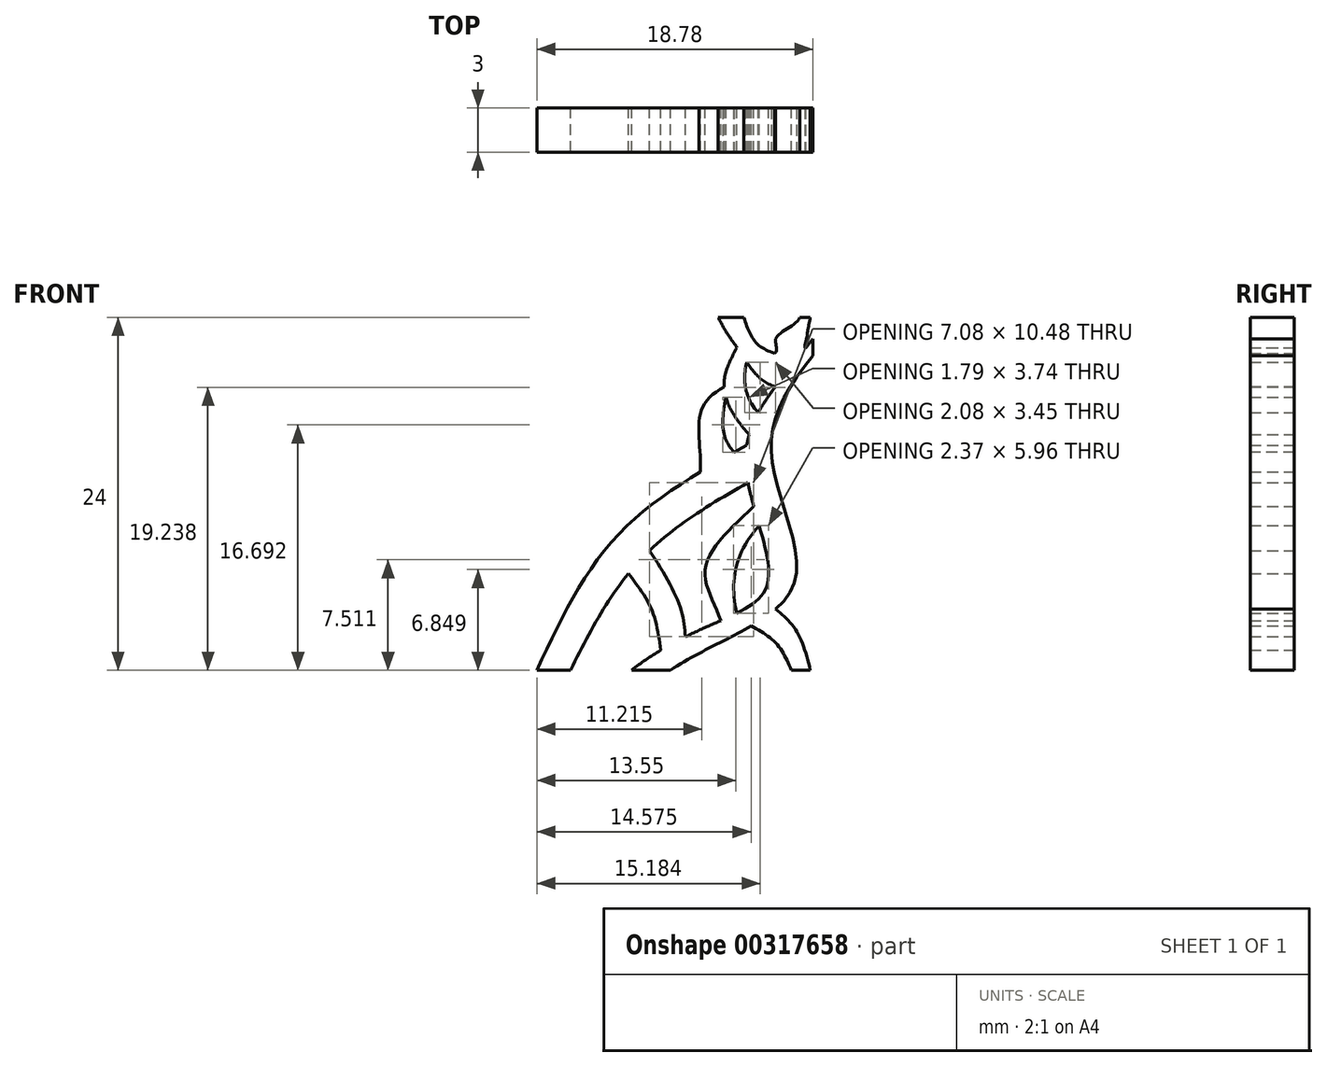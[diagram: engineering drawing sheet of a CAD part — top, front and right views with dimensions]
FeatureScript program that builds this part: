
annotation { "Feature Type Name" : "Feature", "Feature Type Description" : "" }
export const myFeature = defineFeature(function(context is Context, id is Id, definition is map)
    precondition{}
    {
        {
            var Q0;
            Q0=qCreatedBy(makeId("Front.planeOp"),FACE);
            var sketch = newSketch(context, id + "F0", { "sketchPlane" : qUnion([Q0])});
            skLineSegment(sketch, "E0.bottom", {"start": v(161.57, 207.7) * mm, "end": v(-151.57, 207.7) * mm});
            skLineSegment(sketch, "E0.top", {"start": v(161.57, -192.3) * mm, "end": v(-151.57, -192.3) * mm});
            skLineSegment(sketch, "E0.left", {"start": v(161.57, 207.7) * mm, "end": v(161.57, -192.3) * mm});
            skLineSegment(sketch, "E0.right", {"start": v(-151.57, 207.7) * mm, "end": v(-151.57, -192.3) * mm});
            skFitSpline(sketch, "E1", {"points": [v(161.57, 183.5) * mm, v(85.12, 44.75) * mm, v(109.31, -96.4) * mm, v(-44.12, -192.3) * mm], "startDerivative": vector(-382, -492.17) * mm, "endDerivative": vector(-632.26, -490) * mm});
            skFitSpline(sketch, "E2", {"points": [v(161.57, 164.23) * mm, v(115.12, 45.06) * mm, v(139.33, -96.46) * mm, v(0, -192.3) * mm], "startDerivative": vector(-323.93, -389.82) * mm, "endDerivative": vector(-432.8, -289.86) * mm});
            skFitSpline(sketch, "E3", {"points": [v(87.95, 20.15) * mm, v(-36.08, -69.46) * mm, v(-113.36, -192.3) * mm], "startDerivative": vector(-287.2, -159.14) * mm, "endDerivative": vector(-134.26, -271.05) * mm});
            skFitSpline(sketch, "E4", {"points": [v(86.4, 62.77) * mm, v(-60.96, -40.6) * mm, v(-151.57, -192.3) * mm], "startDerivative": vector(-322.1, -181.09) * mm, "endDerivative": vector(-154.33, -329.73) * mm});
            skFitSpline(sketch, "E5", {"points": [v(91.66, -142.16) * mm, v(120.33, -162.57) * mm, v(137.1, -192.3) * mm], "startDerivative": vector(63.12, -36.39) * mm, "endDerivative": vector(28.09, -64.9) * mm});
            skFitSpline(sketch, "E6", {"points": [v(119.32, -123.08) * mm, v(142.68, -147.67) * mm, v(158.5, -192.3) * mm], "startDerivative": vector(55.7, -46.78) * mm, "endDerivative": vector(23.32, -90.23) * mm});
            skFitSpline(sketch, "E7", {"points": [v(100.65, -28.51) * mm, v(73.78, -78.77) * mm, v(75.03, -127.85) * mm], "startDerivative": vector(-88.91, -98.41) * mm, "endDerivative": vector(24.95, -113.83) * mm});
            skFitSpline(sketch, "E8", {"points": [v(94.41, -6.72) * mm, v(39.45, -75.98) * mm, v(57.07, -136.12) * mm], "startDerivative": vector(-135.48, -128.88) * mm, "endDerivative": vector(50.2, -141.27) * mm});
            skFitSpline(sketch, "E9", {"points": [v(54.23, 207.7) * mm, v(81.23, 165.16) * mm, v(119.4, 129.17) * mm], "startDerivative": vector(44.56, -99.42) * mm, "endDerivative": vector(118.17, -31.75) * mm});
            skFitSpline(sketch, "E10", {"points": [v(83.1, 207.7) * mm, v(99.85, 176.33) * mm, v(142.84, 159.86) * mm], "startDerivative": vector(25.78, -76.02) * mm, "endDerivative": vector(99.84, -29.98) * mm});
            skFitSpline(sketch, "E11", {"points": [v(146.4, 207.7) * mm, v(119.4, 183.78) * mm, v(118, 167.02) * mm], "startDerivative": vector(-16.59, -50.41) * mm, "endDerivative": vector(-40.58, -34) * mm});
            skFitSpline(sketch, "E12", {"points": [v(158.5, 207.7) * mm, v(153.85, 181.92) * mm, v(152.97, 172.55) * mm], "startDerivative": vector(-12.64, -48.27) * mm, "endDerivative": vector(10.98, -30.7) * mm});
            skFitSpline(sketch, "E13", {"points": [v(75.43, 173.52) * mm, v(60.75, 128.85) * mm, v(89.2, 75) * mm], "startDerivative": vector(-54.24, -96.72) * mm, "endDerivative": vector(96.14, -103.87) * mm});
            skFitSpline(sketch, "E14", {"points": [v(86.56, 157.05) * mm, v(84.95, 128.85) * mm, v(99.53, 99.55) * mm], "startDerivative": vector(-16.02, -62.32) * mm, "endDerivative": vector(51.54, -60.1) * mm});
            skFitSpline(sketch, "E15", {"points": [v(62.75, 117) * mm, v(60.75, 74.85) * mm, v(72.13, 54.72) * mm], "startDerivative": vector(-16.42, -83.23) * mm, "endDerivative": vector(39.32, -49.75) * mm});
            skFitSpline(sketch, "E16", {"points": [v(60.75, 128.85) * mm, v(35.6, 103.71) * mm, v(32.47, 71.12) * mm, v(33.8, 32.44) * mm], "startDerivative": vector(-112.87, -59.98) * mm, "endDerivative": vector(-6.89, -98.92) * mm});
            skFitSpline(sketch, "E17", {"points": [v(-47.68, -82.88) * mm, v(-21.54, -123.28) * mm, v(-11.06, -169.71) * mm], "startDerivative": vector(59.74, -77.34) * mm, "endDerivative": vector(13.37, -96.33) * mm});
            skFitSpline(sketch, "E18", {"points": [v(-23.58, -56.72) * mm, v(10.06, -118.02) * mm, v(16.93, -154.44) * mm], "startDerivative": vector(70.14, -111.5) * mm, "endDerivative": vector(7.52, -82.35) * mm});
            skSolve(sketch);
        }
        {
            var Q0;
            {var subQ0=sQuery(id+"F0.wireOp",EDGE,"E3");var subQ3=sQuery(id+"F0.wireOp",EDGE,"E1");var subQ4=makeQuery(id+"F0.imprint","INTERSECT",VERTEX,{"derivedFrom":[subQ3,subQ0]});Q0=makeQuery(id+"F0.imprint","IMPRINT",FACE,{"disambiguationData":[TD([[makeQuery(id+"F0.imprint","IMPRINT",EDGE,{"disambiguationData":[TD([[subQ4,1.0]])],"derivedFrom":subQ3}),-1.0]])]});}
            var Q1;
            {var subQ0=sQuery(id+"F0.wireOp",EDGE,"E17");Q1=makeQuery(id+"F0.imprint","IMPRINT",FACE,{"disambiguationData":[TD([[makeQuery(id+"F0.imprint","IMPRINT",EDGE,{"derivedFrom":subQ0}),1.0]])]});}
            var Q2;
            {var subQ0=sQuery(id+"F0.wireOp",EDGE,"E1");var subQ9=sQuery(id+"F0.wireOp",EDGE,"E0.top");var subQ10=makeQuery(id+"F0.imprint","INTERSECT",VERTEX,{"derivedFrom":[subQ9,subQ0]});Q2=makeQuery(id+"F0.imprint","IMPRINT",FACE,{"disambiguationData":[TD([[makeQuery(id+"F0.imprint","IMPRINT",EDGE,{"disambiguationData":[TD([[subQ10,1.0]])],"derivedFrom":subQ9}),-1.0]])]});}
            var Q3;
            {var subQ0=sQuery(id+"F0.wireOp",EDGE,"E5");Q3=makeQuery(id+"F0.imprint","IMPRINT",FACE,{"disambiguationData":[TD([[makeQuery(id+"F0.imprint","IMPRINT",EDGE,{"derivedFrom":subQ0}),1.0]])]});}
            var Q4;
            {var subQ0=sQuery(id+"F0.wireOp",EDGE,"E7");Q4=makeQuery(id+"F0.imprint","IMPRINT",FACE,{"disambiguationData":[TD([[makeQuery(id+"F0.imprint","IMPRINT",EDGE,{"derivedFrom":subQ0}),-1.0]])]});}
            var Q5;
            {var subQ0=sQuery(id+"F0.wireOp",EDGE,"E15");Q5=makeQuery(id+"F0.imprint","IMPRINT",FACE,{"disambiguationData":[TD([[makeQuery(id+"F0.imprint","IMPRINT",EDGE,{"derivedFrom":subQ0}),-1.0]])]});}
            var Q6;
            {var subQ5=sQuery(id+"F0.wireOp",EDGE,"E14");Q6=makeQuery(id+"F0.imprint","IMPRINT",FACE,{"disambiguationData":[TD([[makeQuery(id+"F0.imprint","IMPRINT",EDGE,{"derivedFrom":subQ5}),-1.0]])]});}
            var Q7;
            {var subQ0=sQuery(id+"F0.wireOp",EDGE,"E9");var subQ1=sQuery(id+"F0.wireOp",EDGE,"E0.bottom");var subQ2=makeQuery(id+"F0.imprint","INTERSECT",VERTEX,{"derivedFrom":[subQ1,subQ0]});Q7=makeQuery(id+"F0.imprint","IMPRINT",FACE,{"disambiguationData":[TD([[makeQuery(id+"F0.imprint","IMPRINT",EDGE,{"disambiguationData":[TD([[subQ2,1.0]])],"derivedFrom":subQ1}),1.0]])]});}
            var Q8;
            {var subQ0=sQuery(id+"F0.wireOp",EDGE,"E11");Q8=makeQuery(id+"F0.imprint","IMPRINT",FACE,{"disambiguationData":[TD([[makeQuery(id+"F0.imprint","IMPRINT",EDGE,{"derivedFrom":subQ0}),1.0]])]});}
            extrude(context, id + "F1", {"entities" : qUnion([Q0, Q1, Q2, Q3, Q4, Q5, Q6, Q7, Q8]), "depth" : 50 * mm});
        }
        {
            var Q0;
            Q0=makeQuery(id+"F1.opExtrude","SWEPT_BODY",BODY,{"disambiguationData":[OSD([sQuery(id+"F0.wireOp",EDGE,"E0.bottom"),sQuery(id+"F0.wireOp",EDGE,"E0.top"),sQuery(id+"F0.wireOp",EDGE,"E0.left"),sQuery(id+"F0.wireOp",EDGE,"E1"),sQuery(id+"F0.wireOp",EDGE,"E2"),sQuery(id+"F0.wireOp",EDGE,"E3"),sQuery(id+"F0.wireOp",EDGE,"E4"),sQuery(id+"F0.wireOp",EDGE,"E5"),sQuery(id+"F0.wireOp",EDGE,"E6"),sQuery(id+"F0.wireOp",EDGE,"E7"),sQuery(id+"F0.wireOp",EDGE,"E8"),sQuery(id+"F0.wireOp",EDGE,"E9"),sQuery(id+"F0.wireOp",EDGE,"E10"),sQuery(id+"F0.wireOp",EDGE,"E11"),sQuery(id+"F0.wireOp",EDGE,"E12"),sQuery(id+"F0.wireOp",EDGE,"E13"),sQuery(id+"F0.wireOp",EDGE,"E14"),sQuery(id+"F0.wireOp",EDGE,"E15"),sQuery(id+"F0.wireOp",EDGE,"E16"),sQuery(id+"F0.wireOp",EDGE,"E17"),sQuery(id+"F0.wireOp",EDGE,"E18")])]});
            var Q1;
            Q1=qCreatedBy(makeId("Origin.pointOp"),VERTEX);
            var Q2;
            Q2=qCreatedBy(makeId("Origin.pointOp"),VERTEX);
            transform(context, id + "F2", {"entities" : qUnion([Q0]), "transformType" : TransformType.SCALE_UNIFORMLY, "scale" : 0.06, "scalePoint" : qUnion([Q2]), "makeCopy" : false});
        }
    });
